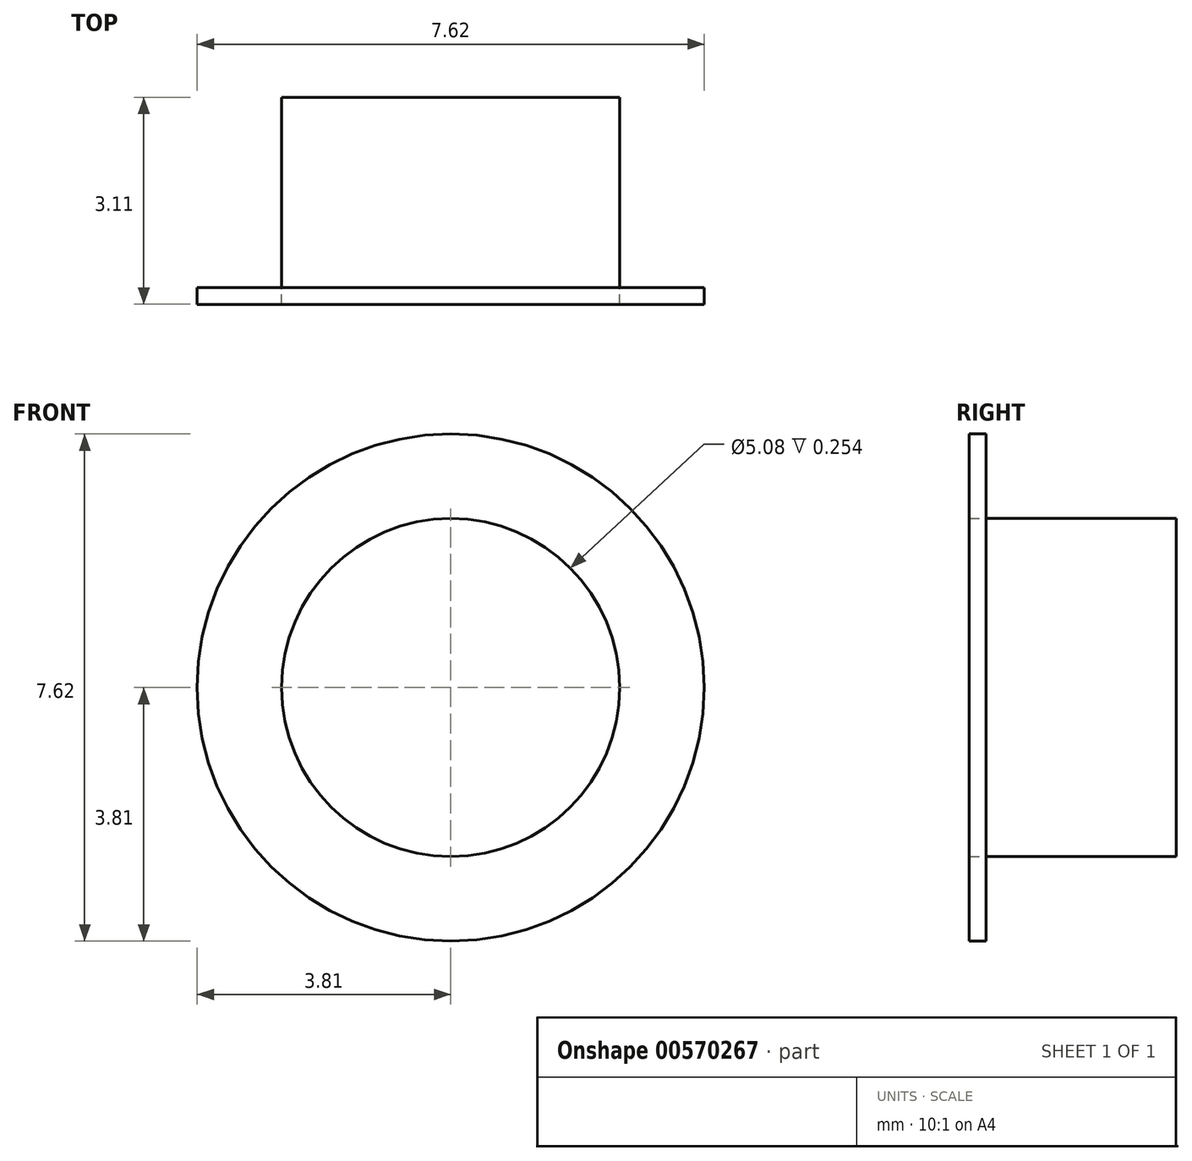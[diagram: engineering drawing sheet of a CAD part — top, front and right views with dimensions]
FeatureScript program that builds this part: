
annotation { "Feature Type Name" : "Feature", "Feature Type Description" : "" }
export const myFeature = defineFeature(function(context is Context, id is Id, definition is map)
    precondition{}
    {
        {
            var Q0;
            Q0=qCreatedBy(makeId("Front.planeOp"),FACE);
            var sketch = newSketch(context, id + "F0", { "sketchPlane" : qUnion([Q0])});
            skCircle(sketch, "E0", {"center": v(0, 0) * mm, "radius": 2.54 * mm});
            skSolve(sketch);
        }
        {
            var Q0;
            Q0=makeQuery(id+"F0.imprint","IMPRINT",FACE,{"disambiguationData":[TD([[makeQuery(id+"F0.imprint","IMPRINT",EDGE,{"derivedFrom":sQuery(id+"F0.wireOp",EDGE,"E0")}),1.0]])]});
            extrude(context, id + "F1", {"entities" : qUnion([Q0]), "endBound" : BoundingType.SYMMETRIC, "depth" : 2.86 * mm, "offsetDistance" : 25.4 * mm});
        }
        {
            var Q0;
            Q0=makeQuery(id+"F1.opExtrude","CAP_FACE",FACE,{"disambiguationData":[OSD([sQuery(id+"F0.wireOp",EDGE,"E0")])],"isStart":false});
            var sketch = newSketch(context, id + "F2", { "sketchPlane" : qUnion([Q0])});
            skCircle(sketch, "E1", {"center": v(0, 0) * mm, "radius": 3.81 * mm});
            skSolve(sketch);
        }
        {
            var Q0;
            Q0=makeQuery(id+"F2.imprint","IMPRINT",FACE,{"disambiguationData":[TD([[makeQuery(id+"F2.imprint","IMPRINT",EDGE,{"derivedFrom":sQuery(id+"F2.wireOp",EDGE,"E1")}),1.0]])]});
            extrude(context, id + "F3", {"entities" : qUnion([Q0]), "operationType" : NewBodyOperationType.ADD, "depth" : 0.25 * mm, "offsetDistance" : 25.4 * mm});
        }
    });
